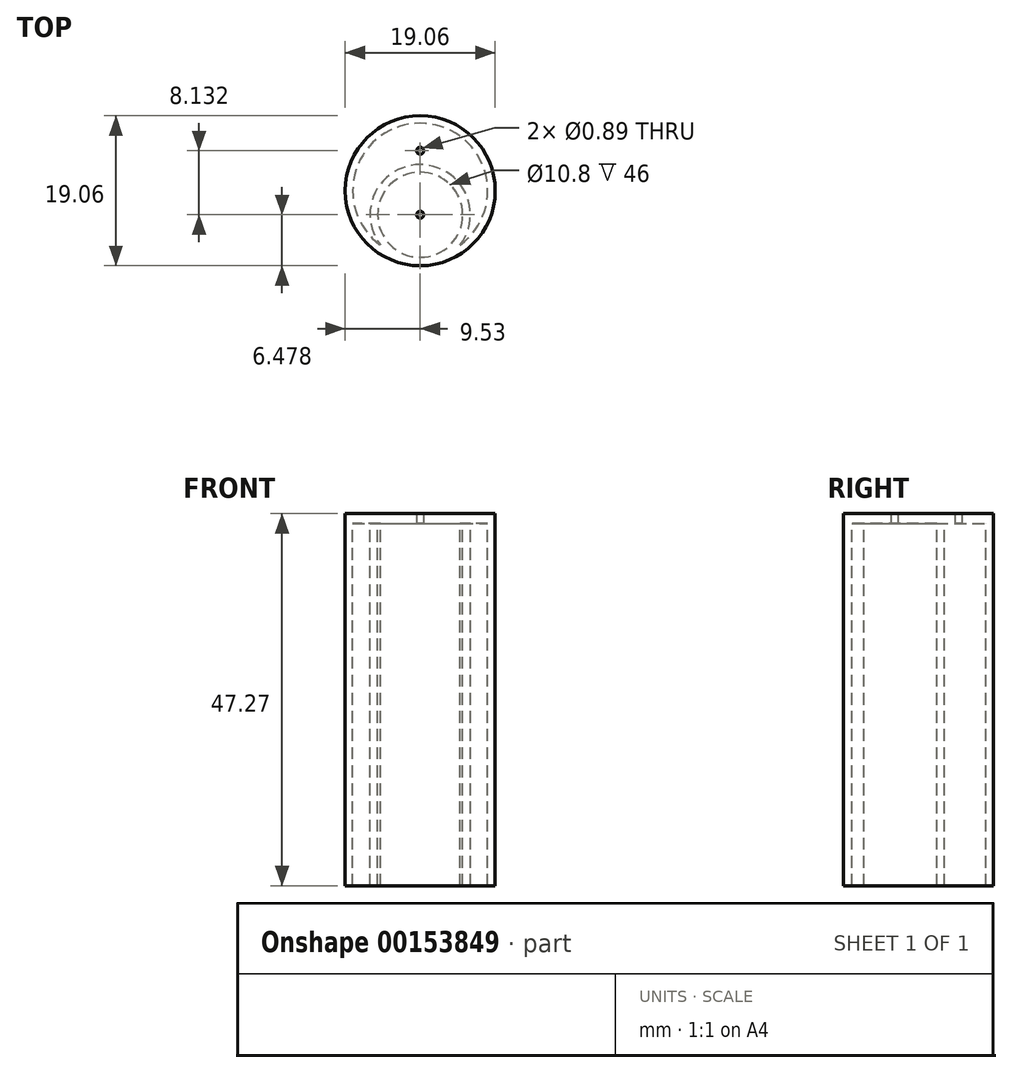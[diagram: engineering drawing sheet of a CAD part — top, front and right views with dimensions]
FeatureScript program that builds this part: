
annotation { "Feature Type Name" : "Feature", "Feature Type Description" : "" }
export const myFeature = defineFeature(function(context is Context, id is Id, definition is map)
    precondition{}
    {
        {
            var Q0;
            Q0=qCreatedBy(makeId("Top.planeOp"),FACE);
            var sketch = newSketch(context, id + "F0", { "sketchPlane" : qUnion([Q0])});
            skCircle(sketch, "E0", {"center": v(0, 0) * mm, "radius": 9.53 * mm});
            skCircle(sketch, "E1.MirrorC", {"center": v(0, -3.05) * mm, "radius": 0.44 * mm});
            skCircle(sketch, "E2", {"center": v(0, 5.08) * mm, "radius": 0.44 * mm});
            skSolve(sketch);
        }
        {
            var Q0;
            Q0 = qSketchRegion(id + "F0", true);
            extrude(context, id + "F1", {"entities" : qUnion([Q0]), "depth" : 2.54 * mm});
        }
        {
            var Q0;
            Q0=makeQuery(id+"F1.opExtrude","CAP_FACE",FACE,{"disambiguationData":[OSD([sQuery(id+"F0.wireOp",EDGE,"E0"),sQuery(id+"F0.wireOp",EDGE,"AFu1EhPd-qrgI-67Gb-cx80-ZaASF7ZTsDt2"),sQuery(id+"F0.wireOp",EDGE,"E1.MirrorC")])],"isStart":false});
            var sketch = newSketch(context, id + "F2", { "sketchPlane" : qUnion([Q0])});
            skCircle(sketch, "E3", {"center": v(0, 0) * mm, "radius": 1.78 * mm});
            skArc(sketch, "E4", {"start": v(9.36, 1.75) * mm, "mid": v(7.71, -0.07) * mm, "end": v(9.33, -1.9) * mm});
            skArc(sketch, "E5.1.0", {"start": v(-1.75, 9.36) * mm, "mid": v(0.07, 7.71) * mm, "end": v(1.9, 9.33) * mm});
            skArc(sketch, "E5.2.0", {"start": v(-9.36, -1.75) * mm, "mid": v(-7.71, 0.07) * mm, "end": v(-9.33, 1.9) * mm});
            skArc(sketch, "E5.3.0", {"start": v(1.75, -9.36) * mm, "mid": v(-0.07, -7.71) * mm, "end": v(-1.9, -9.33) * mm});
            skCircle(sketch, "E6", {"center": v(0, 0) * mm, "radius": 9.52 * mm});
            skSolve(sketch);
        }
        {
            var Q0;
            {var subQ0=sQuery(id+"F2.wireOp",EDGE,"E4");Q0=makeQuery(id+"F2.imprint","IMPRINT",FACE,{"disambiguationData":[TD([[makeQuery(id+"F2.imprint","IMPRINT",EDGE,{"derivedFrom":subQ0}),1.0]])]});}
            var Q1;
            {var subQ0=sQuery(id+"F2.wireOp",EDGE,"E5.1.0");Q1=makeQuery(id+"F2.imprint","IMPRINT",FACE,{"disambiguationData":[TD([[makeQuery(id+"F2.imprint","IMPRINT",EDGE,{"derivedFrom":subQ0}),1.0]])]});}
            var Q2;
            {var subQ0=sQuery(id+"F2.wireOp",EDGE,"E5.2.0");Q2=makeQuery(id+"F2.imprint","IMPRINT",FACE,{"disambiguationData":[TD([[makeQuery(id+"F2.imprint","IMPRINT",EDGE,{"derivedFrom":subQ0}),1.0]])]});}
            var Q3;
            {var subQ0=sQuery(id+"F2.wireOp",EDGE,"E5.3.0");Q3=makeQuery(id+"F2.imprint","IMPRINT",FACE,{"disambiguationData":[TD([[makeQuery(id+"F2.imprint","IMPRINT",EDGE,{"derivedFrom":subQ0}),1.0]])]});}
            var Q4;
            Q4=makeQuery(id+"F2.imprint","IMPRINT",FACE,{"disambiguationData":[TD([[makeQuery(id+"F2.imprint","IMPRINT",EDGE,{"derivedFrom":makeQuery(id+"F1.opExtrude","CAP_EDGE",EDGE,{"disambiguationData":[OSD([sQuery(id+"F0.wireOp",EDGE,"AFu1EhPd-qrgI-67Gb-cx80-ZaASF7ZTsDt2")])],"isStart":false})}),1.0]])]});
            var Q5;
            Q5=makeQuery(id+"F2.imprint","IMPRINT",FACE,{"disambiguationData":[TD([[makeQuery(id+"F2.imprint","IMPRINT",EDGE,{"derivedFrom":makeQuery(id+"F1.opExtrude","CAP_EDGE",EDGE,{"disambiguationData":[OSD([sQuery(id+"F0.wireOp",EDGE,"E1.MirrorC")])],"isStart":false})}),-1.0]])]});
            var Q6;
            Q6=makeQuery(id+"F2.imprint","IMPRINT",FACE,{"disambiguationData":[TD([[makeQuery(id+"F2.imprint","IMPRINT",EDGE,{"derivedFrom":sQuery(id+"F2.wireOp",EDGE,"E3")}),1.0]])]});
            extrude(context, id + "F3", {"entities" : qUnion([Q0, Q1, Q2, Q3, Q4, Q5, Q6]), "operationType" : NewBodyOperationType.REMOVE, "oppositeDirection" : true, "depth" : 1.27 * mm});
        }
        {
            var Q0;
            Q0=makeQuery(id+"F1.opExtrude","CAP_FACE",FACE,{"disambiguationData":[OSD([sQuery(id+"F0.wireOp",EDGE,"E0"),sQuery(id+"F0.wireOp",EDGE,"AFu1EhPd-qrgI-67Gb-cx80-ZaASF7ZTsDt2"),sQuery(id+"F0.wireOp",EDGE,"E1.MirrorC")])],"isStart":true});
            var sketch = newSketch(context, id + "F4", { "sketchPlane" : qUnion([Q0])});
            skCircle(sketch, "E7", {"center": v(0, 0) * mm, "radius": 9.53 * mm});
            skCircle(sketch, "E8", {"center": v(0, 0) * mm, "radius": 8.57 * mm});
            skCircle(sketch, "E9", {"center": v(0, 3.05) * mm, "radius": 5.4 * mm});
            skCircle(sketch, "E10", {"center": v(0, 3.05) * mm, "radius": 6.37 * mm});
            skSolve(sketch);
        }
        {
            var Q0;
            Q0 = qSketchRegion(id + "F4", true);
            var Q1;
            {var subQ0=sQuery(id+"F4.wireOp",EDGE,"E10");var subQ1=sQuery(id+"F4.wireOp",EDGE,"E8");var subQ2=makeQuery(id+"F4.imprint","INTERSECT",VERTEX,{"disambiguationData":[OD(0.0)],"derivedFrom":[subQ1,subQ0]});Q1=makeQuery(id+"F4.imprint","IMPRINT",FACE,{"disambiguationData":[TD([[makeQuery(id+"F4.imprint","IMPRINT",EDGE,{"disambiguationData":[TD([[subQ2,1.0]])],"derivedFrom":subQ1}),-1.0]])]});}
            var Q2;
            Q2=makeQuery(id+"F4.imprint","IMPRINT",FACE,{"disambiguationData":[TD([[makeQuery(id+"F4.imprint","IMPRINT",EDGE,{"derivedFrom":sQuery(id+"F4.wireOp",EDGE,"E9")}),-1.0]])]});
            extrude(context, id + "F5", {"entities" : qUnion([Q0, Q1, Q2]), "operationType" : NewBodyOperationType.ADD, "depth" : 46 * mm});
        }
    });
